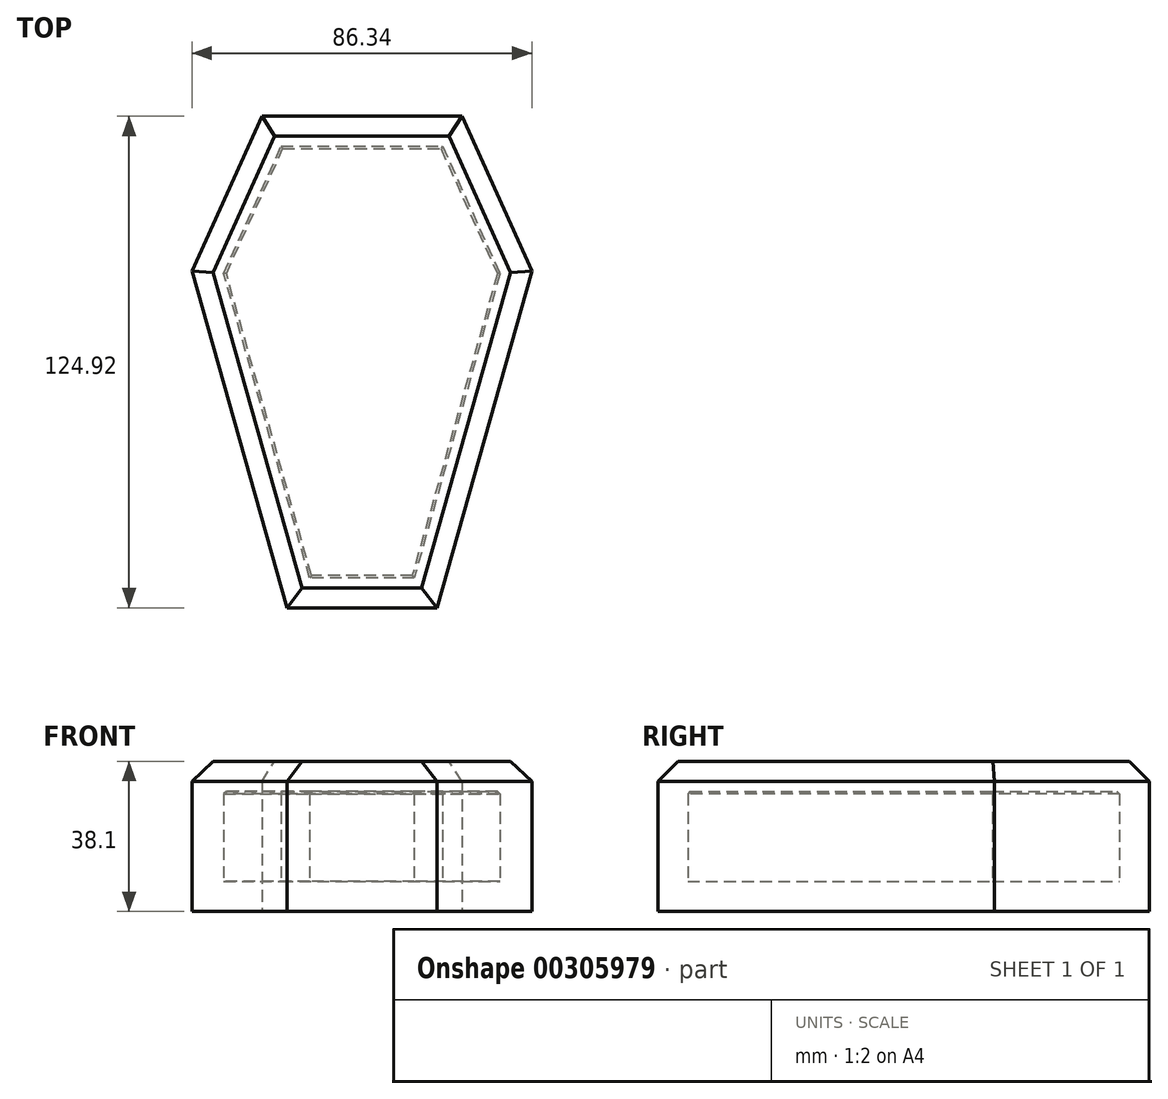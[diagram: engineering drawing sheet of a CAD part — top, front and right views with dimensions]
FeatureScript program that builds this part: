
annotation { "Feature Type Name" : "Feature", "Feature Type Description" : "" }
export const myFeature = defineFeature(function(context is Context, id is Id, definition is map)
    precondition{}
    {
        {
            var Q0;
            Q0=qCreatedBy(makeId("Top.planeOp"),FACE);
            var sketch = newSketch(context, id + "F0", { "sketchPlane" : qUnion([Q0])});
            skLineSegment(sketch, "E0", {"start": v(-32.81, 64.16) * mm, "end": v(17.99, 64.16) * mm});
            skLineSegment(sketch, "E1", {"start": v(17.99, 64.16) * mm, "end": v(35.76, 24.8) * mm});
            skLineSegment(sketch, "E2", {"start": v(35.76, 24.8) * mm, "end": v(11.64, -60.76) * mm});
            skLineSegment(sketch, "E3", {"start": v(11.64, -60.76) * mm, "end": v(-26.46, -60.76) * mm});
            skLineSegment(sketch, "E4", {"start": v(-26.46, -60.76) * mm, "end": v(-50.58, 24.8) * mm});
            skLineSegment(sketch, "E5", {"start": v(-50.58, 24.8) * mm, "end": v(-32.81, 64.16) * mm});
            skSolve(sketch);
        }
        {
            var Q0;
            Q0=makeQuery(id+"F0.imprint","IMPRINT",FACE,{"disambiguationData":[TD([[makeQuery(id+"F0.imprint","IMPRINT",EDGE,{"derivedFrom":sQuery(id+"F0.wireOp",EDGE,"E0")}),-1.0]])]});
            extrude(context, id + "F1", {"entities" : qUnion([Q0]), "depth" : 38.1 * mm});
        }
        {
            var Q0;
            Q0=makeQuery(id+"F1.opExtrude","CAP_EDGE",EDGE,{"disambiguationData":[OSD([sQuery(id+"F0.wireOp",EDGE,"E5")])],"isStart":false});
            var Q1;
            Q1=makeQuery(id+"F1.opExtrude","CAP_EDGE",EDGE,{"disambiguationData":[OSD([sQuery(id+"F0.wireOp",EDGE,"E0")])],"isStart":false});
            var Q2;
            Q2=makeQuery(id+"F1.opExtrude","CAP_EDGE",EDGE,{"disambiguationData":[OSD([sQuery(id+"F0.wireOp",EDGE,"E1")])],"isStart":false});
            var Q3;
            Q3=makeQuery(id+"F1.opExtrude","CAP_EDGE",EDGE,{"disambiguationData":[OSD([sQuery(id+"F0.wireOp",EDGE,"E2")])],"isStart":false});
            var Q4;
            Q4=makeQuery(id+"F1.opExtrude","CAP_EDGE",EDGE,{"disambiguationData":[OSD([sQuery(id+"F0.wireOp",EDGE,"E4")])],"isStart":false});
            var Q5;
            Q5=makeQuery(id+"F1.opExtrude","CAP_EDGE",EDGE,{"disambiguationData":[OSD([sQuery(id+"F0.wireOp",EDGE,"E3")])],"isStart":false});
            chamfer(context, id + "F2", {"entities" : qUnion([Q0, Q1, Q2, Q3, Q4, Q5]), "width" : 5.08 * mm, "tangentPropagation" : true});
        }
        {
            var Q0;
            Q0=makeQuery(id+"F1.opExtrude","CAP_FACE",FACE,{"disambiguationData":[OSD([sQuery(id+"F0.wireOp",EDGE,"E0"),sQuery(id+"F0.wireOp",EDGE,"E1"),sQuery(id+"F0.wireOp",EDGE,"E2"),sQuery(id+"F0.wireOp",EDGE,"E3"),sQuery(id+"F0.wireOp",EDGE,"E4"),sQuery(id+"F0.wireOp",EDGE,"E5")])],"isStart":false});
            var Q1;
            Q1=makeQuery(id+"F1.opExtrude","SWEPT_BODY",BODY,{"disambiguationData":[OSD([sQuery(id+"F0.wireOp",EDGE,"E0"),sQuery(id+"F0.wireOp",EDGE,"E1"),sQuery(id+"F0.wireOp",EDGE,"E2"),sQuery(id+"F0.wireOp",EDGE,"E3"),sQuery(id+"F0.wireOp",EDGE,"E4"),sQuery(id+"F0.wireOp",EDGE,"E5")])]});
            shell(context, id + "F3", {"isHollow" : true, "entities" : qUnion([Q0]), "parts" : qUnion([Q1]), "thickness" : 7.62 * mm});
        }
    });
